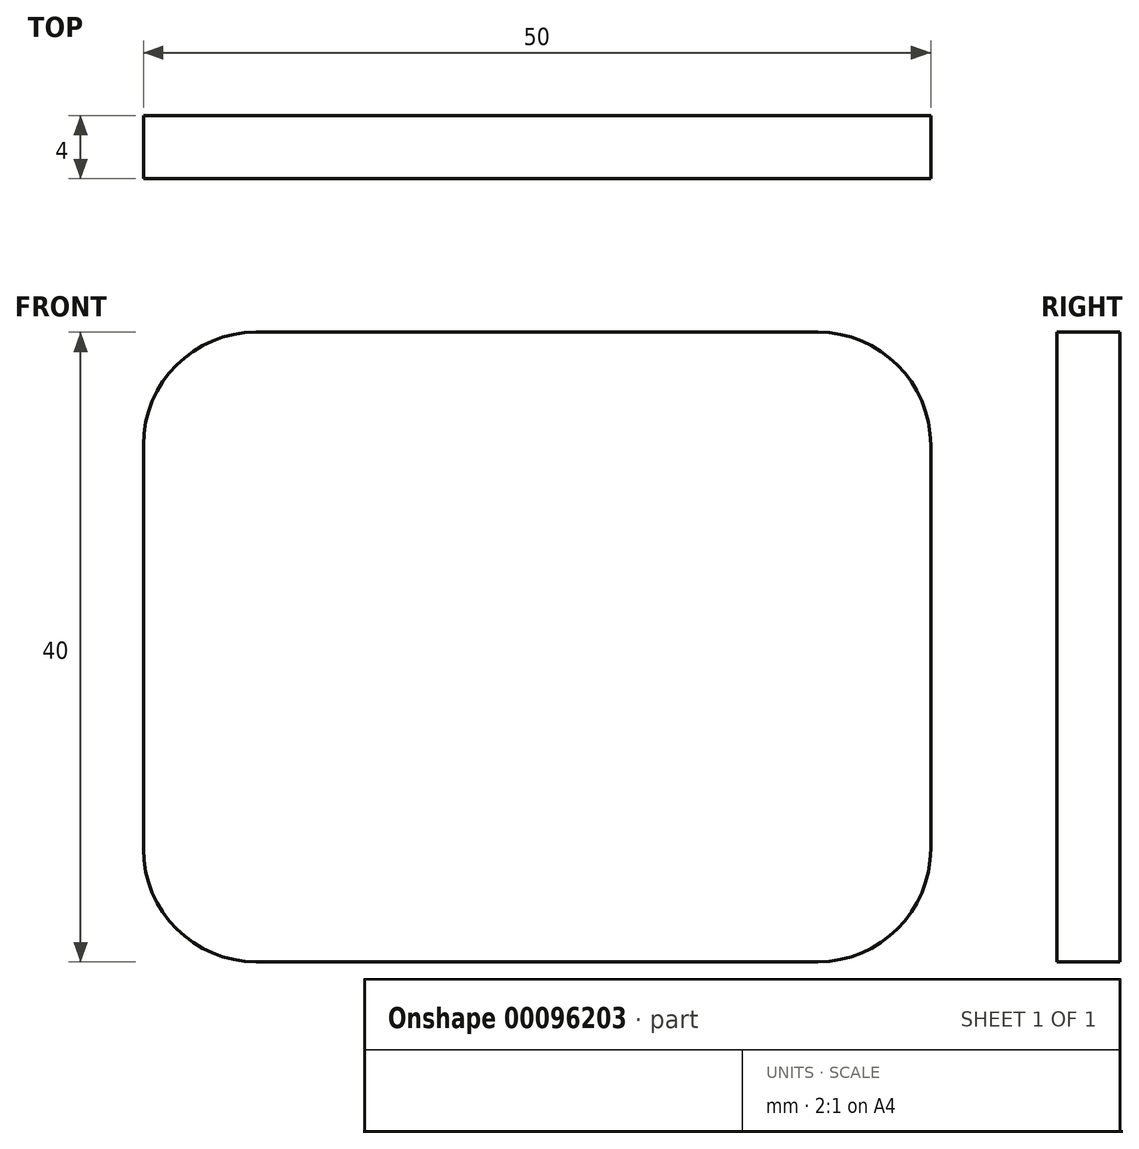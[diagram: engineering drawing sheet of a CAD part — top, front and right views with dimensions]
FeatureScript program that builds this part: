
annotation { "Feature Type Name" : "Feature", "Feature Type Description" : "" }
export const myFeature = defineFeature(function(context is Context, id is Id, definition is map)
    precondition{}
    {
        {
            var Q0;
            Q0=qCreatedBy(makeId("Front.planeOp"),FACE);
            var sketch = newSketch(context, id + "F0", { "sketchPlane" : qUnion([Q0])});
            skLineSegment(sketch, "E0.bottom", {"start": v(-18.5, 19.31) * mm, "end": v(17.16, 19.31) * mm});
            skLineSegment(sketch, "E0.top", {"start": v(-18.5, -20.69) * mm, "end": v(17.16, -20.69) * mm});
            skLineSegment(sketch, "E0.left", {"start": v(-25.67, 12.15) * mm, "end": v(-25.67, -13.52) * mm});
            skLineSegment(sketch, "E0.right", {"start": v(24.33, 12.15) * mm, "end": v(24.33, -13.52) * mm});
            skPoint(sketch, "E1.visualSharp", {"position": v(-25.67, 19.31) * mm});
            skArc(sketch, "E1.filletArc", {"start": v(-18.5, 19.31) * mm, "mid": v(-23.57, 17.22) * mm, "end": v(-25.67, 12.15) * mm});
            skPoint(sketch, "E2.visualSharp", {"position": v(-25.67, -20.69) * mm});
            skArc(sketch, "E2.filletArc", {"start": v(-25.67, -13.52) * mm, "mid": v(-23.57, -18.59) * mm, "end": v(-18.5, -20.69) * mm});
            skPoint(sketch, "E3.visualSharp", {"position": v(24.33, -20.69) * mm});
            skArc(sketch, "E3.filletArc", {"start": v(17.16, -20.69) * mm, "mid": v(22.23, -18.59) * mm, "end": v(24.33, -13.52) * mm});
            skPoint(sketch, "E4.visualSharp", {"position": v(24.33, 19.31) * mm});
            skArc(sketch, "E4.filletArc", {"start": v(24.33, 12.15) * mm, "mid": v(22.23, 17.22) * mm, "end": v(17.16, 19.31) * mm});
            skSolve(sketch);
        }
        {
            var Q0;
            Q0 = qSketchRegion(id + "F0", true);
            extrude(context, id + "F1", {"entities" : qUnion([Q0]), "depth" : 4 * mm});
        }
    });
